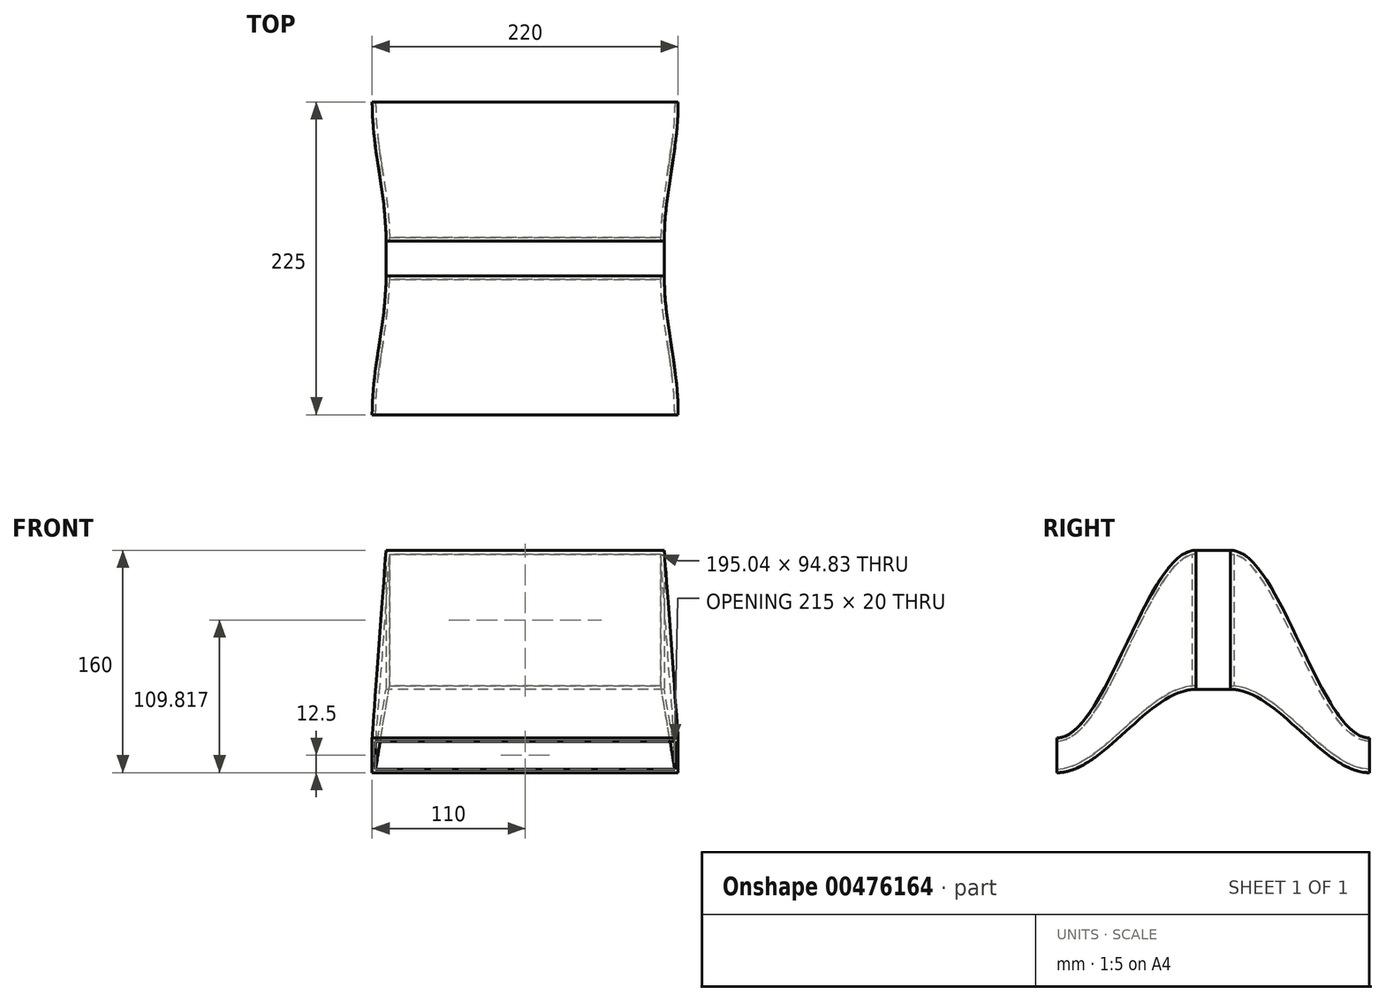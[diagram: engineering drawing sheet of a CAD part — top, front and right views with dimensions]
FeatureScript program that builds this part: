
annotation { "Feature Type Name" : "Feature", "Feature Type Description" : "" }
export const myFeature = defineFeature(function(context is Context, id is Id, definition is map)
    precondition{}
    {
        {
            var Q0;
            Q0=qCreatedBy(makeId("Front.planeOp"),FACE);
            var sketch = newSketch(context, id + "F0", { "sketchPlane" : qUnion([Q0])});
            skLineSegment(sketch, "E0.bottom", {"start": v(100, 50) * mm, "end": v(-100, 50) * mm});
            skLineSegment(sketch, "E0.top", {"start": v(100, -50) * mm, "end": v(-100, -50) * mm});
            skLineSegment(sketch, "E0.left", {"start": v(100, 50) * mm, "end": v(100, -50) * mm});
            skLineSegment(sketch, "E0.right", {"start": v(-100, 50) * mm, "end": v(-100, -50) * mm});
            skPoint(sketch, "E0.middle", {"position": v(0, 0) * mm});
            skSolve(sketch);
        }
        {
            var Q0;
            Q0=makeQuery(id+"F0.imprint","IMPRINT",FACE,{"disambiguationData":[TD([[makeQuery(id+"F0.imprint","IMPRINT",EDGE,{"derivedFrom":sQuery(id+"F0.wireOp",EDGE,"E0.bottom")}),1.0]])]});
            extrude(context, id + "F1", {"entities" : qUnion([Q0]), "oppositeDirection" : true, "depth" : 25 * mm});
        }
        {
            var Q0;
            Q0=qCreatedBy(makeId("Top.planeOp"),FACE);
            cPlane(context, id + "F2", {"entities" : qUnion([Q0]), "cplaneType" : CPlaneType.OFFSET, "offset" : 60 * mm, "oppositeDirection" : true, "width" : 150 * mm, "height" : 150 * mm});
        }
        {
            var Q0;
            Q0=makeQuery(id+"F1.opExtrude","CAP_FACE",FACE,{"disambiguationData":[OSD([sQuery(id+"F0.wireOp",EDGE,"E0.bottom"),sQuery(id+"F0.wireOp",EDGE,"E0.top"),sQuery(id+"F0.wireOp",EDGE,"E0.left"),sQuery(id+"F0.wireOp",EDGE,"E0.right")])],"isStart":true});
            var sketch = newSketch(context, id + "F3", { "sketchPlane" : qUnion([Q0])});
            skLineSegment(sketch, "E1.0", {"start": v(100, 50) * mm, "end": v(-100, 50) * mm});
            skLineSegment(sketch, "E1.1", {"start": v(-100, 50) * mm, "end": v(-100, -50) * mm});
            skLineSegment(sketch, "E1.2", {"start": v(100, -50) * mm, "end": v(-100, -50) * mm});
            skLineSegment(sketch, "E1.3", {"start": v(100, 50) * mm, "end": v(100, -50) * mm});
            skSolve(sketch);
        }
        {
            var Q0;
            Q0=qCreatedBy(id+"F2.planeOp",FACE);
            var sketch = newSketch(context, id + "F4", { "sketchPlane" : qUnion([Q0])});
            skLineSegment(sketch, "E2.0", {"start": v(100, 0) * mm, "end": v(-100, 0) * mm, "construction": true});
            skLineSegment(sketch, "E3", {"start": v(-100, 0) * mm, "end": v(-100, -50) * mm, "construction": true});
            skLineSegment(sketch, "E4", {"start": v(100, 0) * mm, "end": v(100, -50) * mm, "construction": true});
            skLineSegment(sketch, "E5.bottom", {"start": v(-100, -50) * mm, "end": v(100, -50) * mm});
            skLineSegment(sketch, "E5.top", {"start": v(-100, -130) * mm, "end": v(100, -130) * mm});
            skLineSegment(sketch, "E5.left", {"start": v(-100, -50) * mm, "end": v(-100, -130) * mm});
            skLineSegment(sketch, "E5.right", {"start": v(100, -50) * mm, "end": v(100, -130) * mm});
            skSolve(sketch);
        }
        {
            var Q1;
            Q1=makeQuery(id+"F4.imprint","IMPRINT",FACE,{"disambiguationData":[TD([[makeQuery(id+"F4.imprint","IMPRINT",EDGE,{"derivedFrom":sQuery(id+"F4.wireOp",EDGE,"E5.bottom")}),-1.0]])]});
            var Q2;
            Q2=makeQuery(id+"F3.imprint","IMPRINT",FACE,{"disambiguationData":[TD([[makeQuery(id+"F3.imprint","IMPRINT",EDGE,{"derivedFrom":sQuery(id+"F3.wireOp",EDGE,"E1.0")}),1.0]])]});
            loft(context, id + "F5", {"startCondition" : LoftEndDerivativeType.NORMAL_TO_PROFILE, "startMagnitude" : 1, "sheetProfilesArray" : [{ "sheetProfileEntities" : qUnion([Q1]) }, { "sheetProfileEntities" : qUnion([Q2]) }]});
        }
        {
            var Q0;
            Q0=qCreatedBy(makeId("Front.planeOp"),FACE);
            cPlane(context, id + "F6", {"entities" : qUnion([Q0]), "cplaneType" : CPlaneType.OFFSET, "offset" : 100 * mm, "width" : 150 * mm, "height" : 150 * mm});
        }
        {
            var Q0;
            Q0=qCreatedBy(id+"F6.planeOp",FACE);
            var sketch = newSketch(context, id + "F7", { "sketchPlane" : qUnion([Q0])});
            skLineSegment(sketch, "E6.0", {"start": v(-100, -60) * mm, "end": v(100, -60) * mm, "construction": true});
            skLineSegment(sketch, "E7.0", {"start": v(-110, -85) * mm, "end": v(110, -85) * mm});
            skLineSegment(sketch, "E8", {"start": v(-110, -85) * mm, "end": v(-110, -110) * mm});
            skLineSegment(sketch, "E9", {"start": v(-110, -110) * mm, "end": v(110, -110) * mm});
            skLineSegment(sketch, "E10", {"start": v(110, -110) * mm, "end": v(110, -85) * mm});
            skLineSegment(sketch, "E11", {"start": v(0, -60) * mm, "end": v(0, -110) * mm, "construction": true});
            skSolve(sketch);
        }
        {
            var Q1;
            Q1=makeQuery(id+"F7.imprint","IMPRINT",FACE,{"disambiguationData":[TD([[makeQuery(id+"F7.imprint","IMPRINT",EDGE,{"derivedFrom":sQuery(id+"F7.wireOp",EDGE,"E7.0")}),-1.0]])]});
            var Q2;
            Q2=makeQuery(id+"F1.opExtrude","CAP_FACE",FACE,{"disambiguationData":[OSD([sQuery(id+"F0.wireOp",EDGE,"E0.bottom"),sQuery(id+"F0.wireOp",EDGE,"E0.top"),sQuery(id+"F0.wireOp",EDGE,"E0.left"),sQuery(id+"F0.wireOp",EDGE,"E0.right")])],"isStart":true});
            loft(context, id + "F8", {"startCondition" : LoftEndDerivativeType.NORMAL_TO_PROFILE, "startMagnitude" : 1, "endCondition" : LoftEndDerivativeType.MATCH_TANGENT, "endMagnitude" : 1, "sheetProfilesArray" : [{ "sheetProfileEntities" : qUnion([Q1]) }, { "sheetProfileEntities" : qUnion([Q2]) }]});
        }
        {
            var Q0;
            Q0=makeQuery(id+"F8.opLoft","CAP_FACE",FACE,{"disambiguationData":[OSD([makeQuery(id+"F7.imprint","IMPRINT",FACE,{"disambiguationData":[TD([[makeQuery(id+"F7.imprint","IMPRINT",EDGE,{"derivedFrom":sQuery(id+"F7.wireOp",EDGE,"E7.0")}),-1.0]])]})])],"isStart":true});
            shell(context, id + "F9", {"entities" : qUnion([Q0]), "thickness" : 2.5 * mm});
        }
        {
            var Q0;
            Q0=makeQuery(id+"F9.opShell","OFFSET_FACE",FACE,{"disambiguationData":[OSD([sQuery(id+"F0.wireOp",EDGE,"E0.bottom"),sQuery(id+"F0.wireOp",EDGE,"E0.top"),sQuery(id+"F0.wireOp",EDGE,"E0.left"),sQuery(id+"F0.wireOp",EDGE,"E0.right")])]});
            extrude(context, id + "F10", {"entities" : qUnion([Q0]), "operationType" : NewBodyOperationType.REMOVE, "endBound" : BoundingType.UP_TO_NEXT, "oppositeDirection" : true, "depth" : 25 * mm});
        }
        {
            var Q0;
            Q0=makeQuery(id+"F5.opLoft","SWEPT_BODY",BODY,{"disambiguationData":[OSD([makeQuery(id+"F3.imprint","IMPRINT",FACE,{"disambiguationData":[TD([[makeQuery(id+"F3.imprint","IMPRINT",EDGE,{"derivedFrom":sQuery(id+"F3.wireOp",EDGE,"E1.0")}),1.0]])]}),makeQuery(id+"F4.imprint","IMPRINT",FACE,{"disambiguationData":[TD([[makeQuery(id+"F4.imprint","IMPRINT",EDGE,{"derivedFrom":sQuery(id+"F4.wireOp",EDGE,"E5.bottom")}),-1.0]])]})])]});
            deleteBodies(context, id + "F11", {"entities" : qUnion([Q0])});
        }
        {
            var Q0;
            Q0=makeQuery(id+"F8.opLoft","SWEPT_BODY",BODY,{"disambiguationData":[OSD([sQuery(id+"F0.wireOp",EDGE,"E0.bottom"),sQuery(id+"F0.wireOp",EDGE,"E0.top"),sQuery(id+"F0.wireOp",EDGE,"E0.left"),sQuery(id+"F0.wireOp",EDGE,"E0.right"),makeQuery(id+"F7.imprint","IMPRINT",FACE,{"disambiguationData":[TD([[makeQuery(id+"F7.imprint","IMPRINT",EDGE,{"derivedFrom":sQuery(id+"F7.wireOp",EDGE,"E7.0")}),-1.0]])]})])]});
            var Q1;
            Q1=qCreatedBy(makeId("Front.planeOp"),FACE);
            mirror(context, id + "F12", {"entities" : qUnion([Q0]), "mirrorPlane" : qUnion([Q1])});
        }
        {
            var Q0;
            Q0=makeQuery(id+"F12.opPattern","COPY",BODY,{"derivedFrom":makeQuery(id+"F8.opLoft","SWEPT_BODY",BODY,{"disambiguationData":[OSD([sQuery(id+"F0.wireOp",EDGE,"E0.bottom"),sQuery(id+"F0.wireOp",EDGE,"E0.top"),sQuery(id+"F0.wireOp",EDGE,"E0.left"),sQuery(id+"F0.wireOp",EDGE,"E0.right"),makeQuery(id+"F7.imprint","IMPRINT",FACE,{"disambiguationData":[TD([[makeQuery(id+"F7.imprint","IMPRINT",EDGE,{"derivedFrom":sQuery(id+"F7.wireOp",EDGE,"E7.0")}),-1.0]])]})])]}),"instanceName":"1"});
            var Q1;
            Q1=makeQuery(id+"F1.opExtrude","SWEPT_EDGE",EDGE,{"disambiguationData":[OSD([sQuery(id+"F0.wireOp",EDGE,"E0.bottom"),sQuery(id+"F0.wireOp",EDGE,"E0.left")])]});
            transform(context, id + "F13", {"entities" : qUnion([Q0]), "transformType" : TransformType.TRANSLATION_DISTANCE, "transformDirection" : qUnion([Q1]), "distance" : 25 * mm, "oppositeDirection" : true, "makeCopy" : false});
        }
    });
